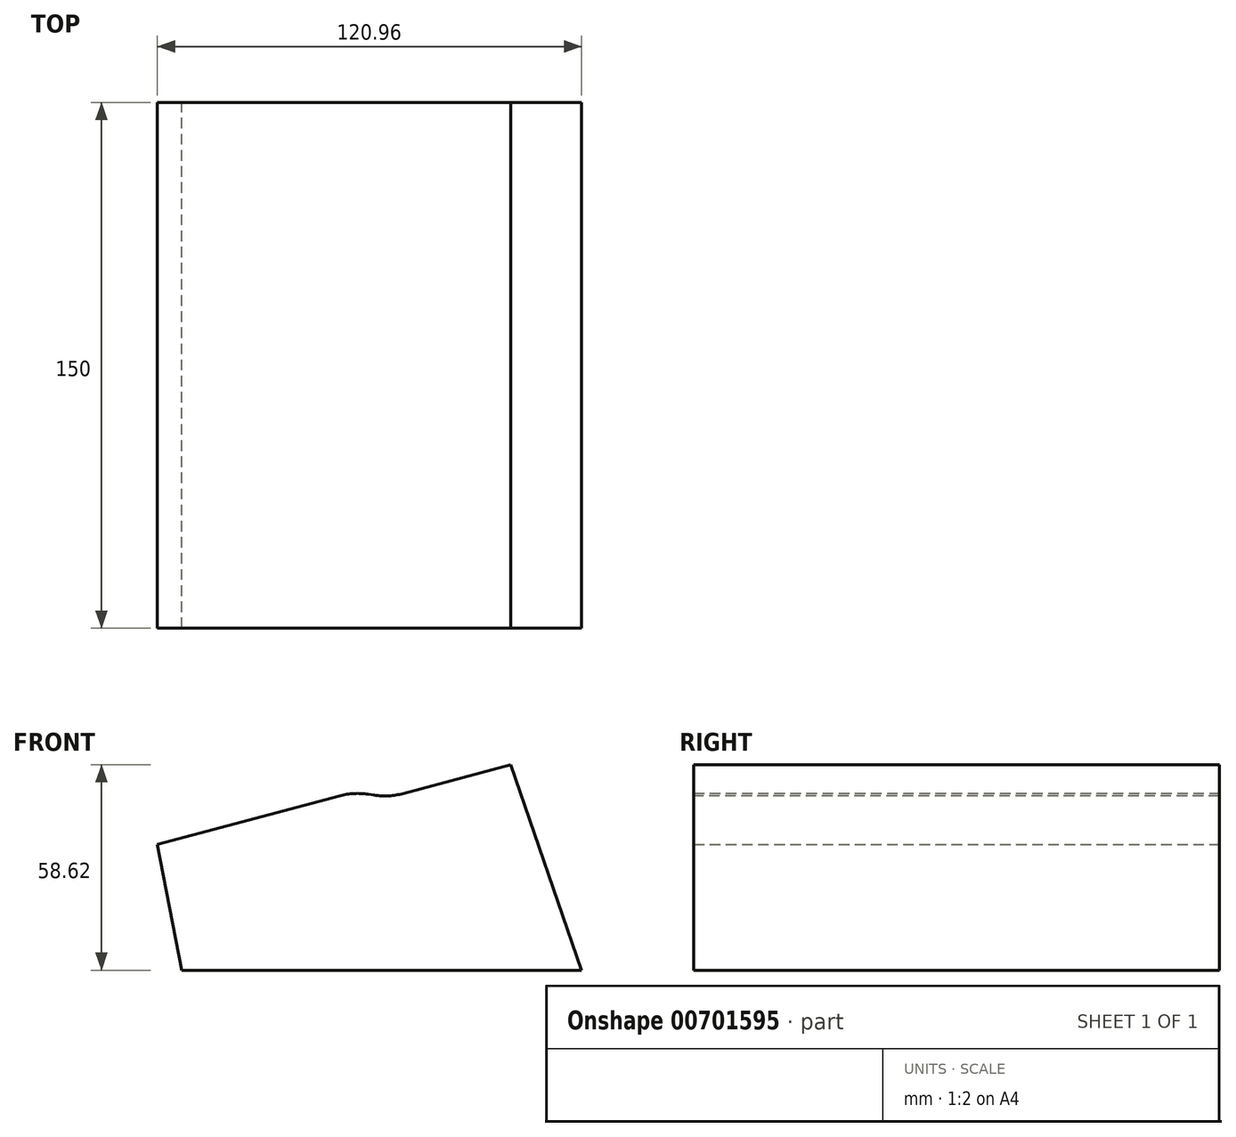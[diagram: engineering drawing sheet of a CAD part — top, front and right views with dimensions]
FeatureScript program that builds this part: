
annotation { "Feature Type Name" : "Feature", "Feature Type Description" : "" }
export const myFeature = defineFeature(function(context is Context, id is Id, definition is map)
    precondition{}
    {
        {
            var Q0;
            Q0=qCreatedBy(makeId("Front.planeOp"),FACE);
            var sketch = newSketch(context, id + "F0", { "sketchPlane" : qUnion([Q0])});
            skLineSegment(sketch, "E0", {"start": v(0, 0) * mm, "end": v(114, 0) * mm});
            skLineSegment(sketch, "E1", {"start": v(114, 0) * mm, "end": v(93.81, 58.62) * mm});
            skLineSegment(sketch, "E2", {"start": v(93.81, 58.62) * mm, "end": v(59.04, 49.3) * mm});
            skLineSegment(sketch, "E3", {"start": v(59.04, 49.3) * mm, "end": v(49.06, 50.84) * mm});
            skLineSegment(sketch, "E4", {"start": v(49.06, 50.84) * mm, "end": v(-6.96, 35.83) * mm});
            skLineSegment(sketch, "E5", {"start": v(-6.96, 35.83) * mm, "end": v(0, 0) * mm});
            skSolve(sketch);
        }
        {
            var Q0;
            Q0 = qSketchRegion(id + "F0", true);
            extrude(context, id + "F1", {"entities" : qUnion([Q0]), "endBound" : BoundingType.SYMMETRIC, "depth" : 150 * mm, "offsetDistance" : 25 * mm});
        }
        {
            var Q0;
            Q0=makeQuery(id+"F1.opExtrude","SWEPT_EDGE",EDGE,{"disambiguationData":[OSD([sQuery(id+"F0.wireOp",EDGE,"E3"),sQuery(id+"F0.wireOp",EDGE,"E4")])]});
            var Q1;
            Q1=makeQuery(id+"F1.opExtrude","SWEPT_EDGE",EDGE,{"disambiguationData":[OSD([sQuery(id+"F0.wireOp",EDGE,"E2"),sQuery(id+"F0.wireOp",EDGE,"E3")])]});
            fillet(context, id + "F2", {"entities" : qUnion([Q0, Q1]), "radius" : 20 * mm, "tangentPropagation" : true, "allowEdgeOverflow" : false});
        }
    });
